# Revit family: Franke_S700_TS_FW(JP)
name_source: partatom
category: Specialty Equipment
revit_build: Autodesk Revit 2015 (Build: 20140606_1530(x64)
units: mm (PartAtom-declared; Revit-internal decimal feet)

## types (2) — shared parameters
Cycle = 50 Hz
Cycle Alternative = 60 Hz
Depth Actual = 600 mm
Description = fully automatic coffee machine
Energy loss acc. to DIN 18873 = - kWh/24h - 400 V 16 A
Height Actual = 796 mm  [stored 2.61155 ft]
Incoming water (cold water) = 8.00 mm
Length Actual = 340 mm  [stored 1.11549 ft]
Manufacturer = Franke Coffee Systems
Max Overcurrent Protection = 30 A
Model = S700 TS FW
Noise emission = 70 dB
Number of Nutral Conductors = 0
Number of Poles = 3
Number of Protective Conductors = 1
URL = https://www.franke.com
Volts max. = 220 V
Volts min. = 200 V
Wastewater = 16.00 mm
Water pressure = 800000.0 Pa
Water pressure (with filter) = 600000.0 Pa
Watts max. = 8000 W
Watts min. = 6800 W
Weight = 58.00 kg

## per-type parameters (varying)
| type | Frontcover |
| S700 TS FW (200-220V/anthracite/JP) | Franke Anthracite |
| S700 TS FW (200-220V/black line/JP) | Franke Black |

note: [stored X ft] marks values corroborated as IEEE doubles in the binary element streams (Revit-internal decimal feet)
